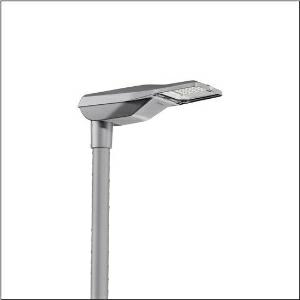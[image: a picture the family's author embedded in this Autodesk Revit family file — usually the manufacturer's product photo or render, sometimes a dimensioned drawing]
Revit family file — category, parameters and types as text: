
# Revit family: streetlight_sl_21_iq_micro___st1_5a_5xe1p41d08cb_4bae
name_source: partatom
category: Lighting Fixtures
units: mm (PartAtom-declared; Revit-internal decimal feet)

## family parameters
Cut with Voids When Loaded = No
Host = Face
Light Source = No
Part Type = Normal
Room Calculation Point = No
Round Connector Dimension = Use Diameter
Shared = No

## types (1)
- --- (1 x LED, 2930 lm, 19.4 W, 4000K)
    Apparent Load = 19 VA
    CIE Flux Codes = 22 53 95 100 100
    Color Rendering = 70
    Color Temperature = 4000K
    Default Elevation = 1800 mm
    Description = Streetlight SL 21 iQ micro, mast luminaire, primary light control with lens, of PMMA, primary optical cover: cover, of toughened safety glass, transparent, light distribution: ST1.5a, light emission: direct distribution, primary light characteristic: asymmetric, installation type: post-top, side-entry, LED, High Power LED, rated luminous flux: 2.930lm, luminous efficacy: 151lm/W, light colour: 740, colour temperature: 4000K, control gear: iQ-Comfort, control: Auto-Match, Temp-Guard, Lumen-Switch, Night-Set, Smart-Wire, Light-Fading, Desk-Remote (wireless, voltage-free reading and setting of iQ features in the workshop via application-optimized NFC function/RFID function), optimised constant luminous flux control (CLO 2.0), pre-setting: linear dimming characteristic, mains connection: 220..240V, AC, 50/60Hz, start of lifetime: 19W, end of service life: 20W, reduction: 10W, luminaire housing, of diecast aluminium, powder-coated, SITECO metallic grey (DB 702S), corrosivity category C5 high according to DIN EN ISO 12944, please order mast flange separately, inclination adjustable: 0°, 5°, 10°, 15°, sealing non-destructively replaceable, multi-level sealing system, length: 528mm, width: 235mm, height: 110mm, mast flange for spigot size: 42mm (side-entry): 5XC10008XM4, 60/48mm (side-entry/post-top): 5XC10108XM2, 76/60mm (side-entry/post-top): 5XC10108XM1, protection rating (complete): IP66, insulation class (complete): insulation class II (safety insulation), certification: CE, ENEC, ENEC+, VDE, impact resistance: IK10, permissible operating ambient temperature for outdoor applications: -40..+50°C, standard-compliant lighting for roads and squares, packaging unit: 1 piece

Light Distribution: ST1.5a
    Height = 110 mm
    Lamp = 1 x LED
    Lamp Light Flux = 2930 lm
    Lamp Power = 19.4 W
    Lamp count = 1
    Length = 528 mm
    Luminous efficacy = 151 lm/W
    Manufacturer = Siteco
    ModVariant = No
    Model = 5XE1P41D08CB
    Number of Poles = 1
    OnlyDefault = Yes
    Power Factor = 1
    Product Name = Streetlight SL 21 iQ micro | ST1.5a
    Product group = mast luminaire | pylon top
    ProductGroupID = 6100
    Protection Class = Protection class II
    Protection Degree = IP 66
    RLX_Detail_Level = 1
    RLX_Emergency_Light_Flux = 0 lm
    RLX_Emergency_Type = 0
    RLX_Emergency_Type_DB = No
    RlxData = <blob elided: 102701 chars, md5=d0862c9d>
    Socket = socket
    Standby Power = 0 W
    System Light Flux = 2930 lm
    System Power = 19 W
    Type Comments = factory setting: luminous flux: 100 % | dim-lin: 254 | 387 mA
    Type Image = l_1006881.jpg
    URL = http://relux.com
    VarID = @adj_137531
    Voltage = 0 V
    Weight = 0.00 kg
    Width = 235 mm

## geometry (parser evidence)
native form markers: Blend x4, Sweep x12
no freeform markers — native parametric forms only
